# Revit family: Lockin Lockers AU_EOT Extras_R22
name_source: partatom
category: Furniture
units: mm (PartAtom-declared; Revit-internal decimal feet)

## family parameters
Always vertical = Yes
Cut with Voids When Loaded = No
OmniClass Number = 23.40.20.27
OmniClass Title = Storage Shelving
Render Appearance Source = Family Geometry
Room Calculation Point = No
Shared = Yes
Work Plane-Based = Yes

## types (7) — shared parameters
Body/Frame Material = Material - Melamine - Laminex or Polytec Finish
Door Material = Material - Melamine - Laminex or Polytec Finish
Manufacturer = Lockin Lockers AU
URL = https://www.lockin.com.au
zero-valued in all types: Default Elevation

## per-type parameters (varying)
| type | Description | EOT Type | Model |
| Airing Cupboard (AC) | Airing Cupboard | Lockin Lockers AU_Airing Cupboard_R22 : Airing Cupboard (AC) | AC |
| Ironing Board (IB) | Ironing Board | Lockin Lockers AU_Ironing Board_R22 : Ironing Board (IB) | IB |
| Umbrella Cupboard (UC) | Umbrella Cupboard | Lockin Lockers AU_Umbrella Cupboard_R22 : Umbrella Cupboard (UC) | UC |
| Towel Storage Unit - Circular Hole (TS) | Towel Storage Unit | Lockin Lockers AU_Towel Storage Unit_R22 : Towel Storage Unit - Circular Hole (TS) | TS |
| Towel Storage Unit - Rectangular Hole (TS) | Towel Storage Unit | Lockin Lockers AU_Towel Storage Unit_R22 : Towel Storage Unit - Rectangular Hole (TS) | TS |
| Towel Storage Unit - Rectangular Hole w/ Door (TS) | Towel Storage Unit | Lockin Lockers AU_Towel Storage Unit_R22 : Towel Storage Unit - Rectangular Hole w/ Door (TS) | TS |
| DDA Ironing Board (ALIB) | DDA Ironing Board | Lockin Lockers AU_Ironing Board_R22 : DDA Ironing board (ALIB) | ALIB |

## geometry (parser evidence)
native form markers: Sweep x15
no freeform markers — native parametric forms only
